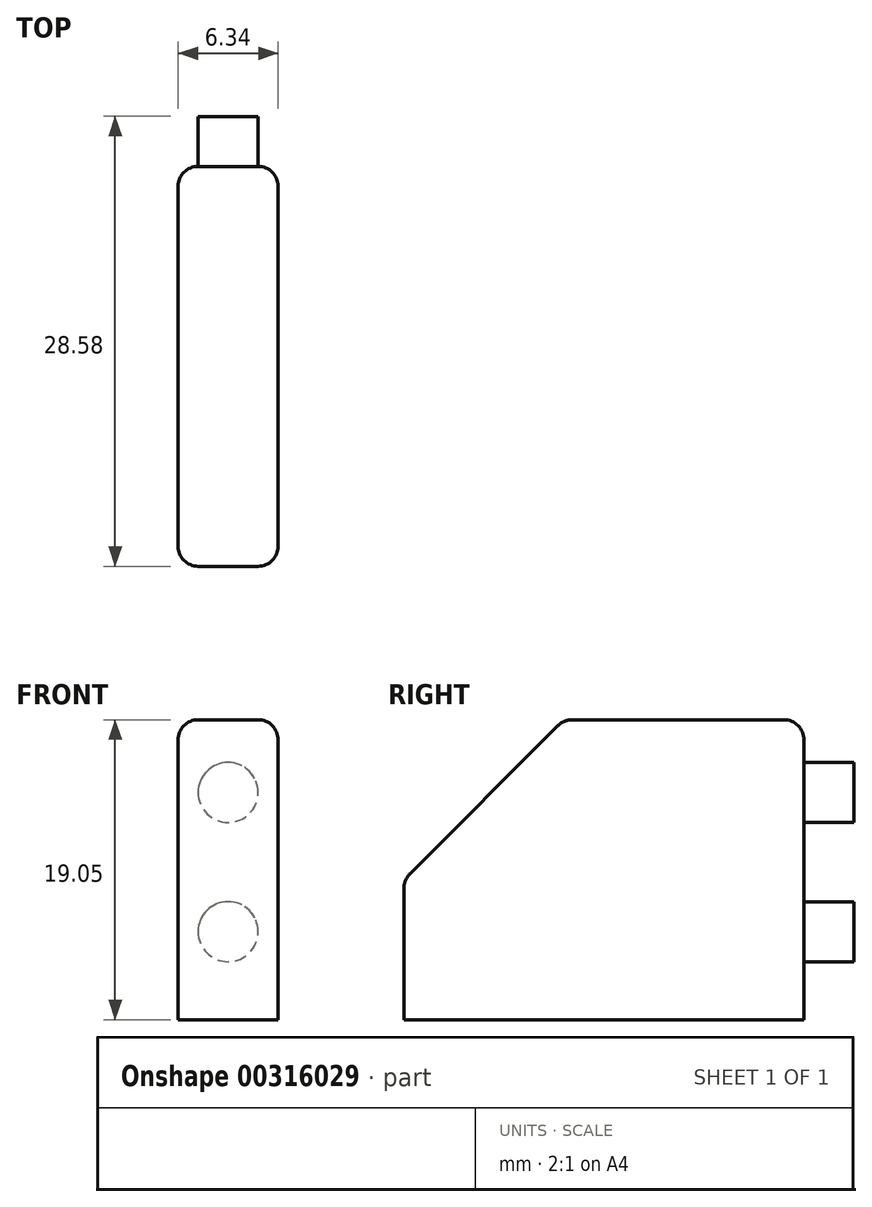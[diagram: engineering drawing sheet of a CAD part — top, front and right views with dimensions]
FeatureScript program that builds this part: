
annotation { "Feature Type Name" : "Feature", "Feature Type Description" : "" }
export const myFeature = defineFeature(function(context is Context, id is Id, definition is map)
    precondition{}
    {
        {
            var Q0;
            Q0=qCreatedBy(makeId("Top.planeOp"),FACE);
            var sketch = newSketch(context, id + "F0", { "sketchPlane" : qUnion([Q0])});
            skLineSegment(sketch, "E0.bottom", {"start": v(3.18, 12.7) * mm, "end": v(-3.17, 12.7) * mm});
            skLineSegment(sketch, "E0.top", {"start": v(3.18, -12.7) * mm, "end": v(-3.18, -12.7) * mm});
            skLineSegment(sketch, "E0.left", {"start": v(3.18, 12.7) * mm, "end": v(3.18, -12.7) * mm});
            skLineSegment(sketch, "E0.right", {"start": v(-3.17, 12.7) * mm, "end": v(-3.18, -12.7) * mm});
            skPoint(sketch, "E0.middle", {"position": v(0, 0) * mm});
            skSolve(sketch);
        }
        {
            var Q0;
            Q0 = qSketchRegion(id + "F0", true);
            extrude(context, id + "F1", {"entities" : qUnion([Q0]), "depth" : 19.05 * mm});
        }
        {
            var Q0;
            Q0=makeQuery(id+"F1.opExtrude","CAP_EDGE",EDGE,{"disambiguationData":[OSD([sQuery(id+"F0.wireOp",EDGE,"E0.top")])],"isStart":false});
            chamfer(context, id + "F2", {"entities" : qUnion([Q0]), "width" : 10.16 * mm, "tangentPropagation" : true});
        }
        {
            var Q0;
            Q0=makeQuery(id+"F1.opExtrude","CAP_EDGE",EDGE,{"disambiguationData":[OSD([sQuery(id+"F0.wireOp",EDGE,"E0.bottom")])],"isStart":false});
            var Q1;
            {var subQ0=sQuery(id+"F0.wireOp",EDGE,"E0.top");Q1=makeQuery(id+"F2.opChamfer","BLEND_EDGE",EDGE,{"blendedFrom":[makeQuery(id+"F1.opExtrude","CAP_EDGE",EDGE,{"disambiguationData":[OSD([subQ0])],"isStart":false}),makeQuery(id+"F1.opExtrude","CAP_FACE",FACE,{"disambiguationData":[OSD([sQuery(id+"F0.wireOp",EDGE,"E0.bottom"),subQ0,sQuery(id+"F0.wireOp",EDGE,"E0.left"),sQuery(id+"F0.wireOp",EDGE,"E0.right")])],"isStart":false})],"blendedInto":[makeQuery(id+"F1.opExtrude","CAP_FACE",FACE,{"disambiguationData":[OSD([sQuery(id+"F0.wireOp",EDGE,"E0.bottom"),subQ0,sQuery(id+"F0.wireOp",EDGE,"E0.left"),sQuery(id+"F0.wireOp",EDGE,"E0.right")])],"isStart":false})]});}
            var Q2;
            {var subQ0=sQuery(id+"F0.wireOp",EDGE,"E0.top");Q2=makeQuery(id+"F2.opChamfer","BLEND_EDGE",EDGE,{"blendedFrom":[makeQuery(id+"F1.opExtrude","CAP_EDGE",EDGE,{"disambiguationData":[OSD([subQ0])],"isStart":false}),makeQuery(id+"F1.opExtrude","SWEPT_FACE",FACE,{"disambiguationData":[OSD([subQ0])]})],"blendedInto":[makeQuery(id+"F1.opExtrude","SWEPT_FACE",FACE,{"disambiguationData":[OSD([subQ0])]})]});}
            fillet(context, id + "F3", {"entities" : qUnion([Q0, Q1, Q2]), "radius" : 1.27 * mm, "tangentPropagation" : true, "allowEdgeOverflow" : false});
        }
        {
            var Q0;
            Q0=makeQuery(id+"F1.opExtrude","SWEPT_EDGE",EDGE,{"disambiguationData":[OSD([sQuery(id+"F0.wireOp",EDGE,"E0.top"),sQuery(id+"F0.wireOp",EDGE,"E0.left")])]});
            var Q1;
            Q1=makeQuery(id+"F2.opChamfer","BLEND_EDGE",EDGE,{"blendedFrom":[makeQuery(id+"F1.opExtrude","CAP_EDGE",EDGE,{"disambiguationData":[OSD([sQuery(id+"F0.wireOp",EDGE,"E0.top")])],"isStart":false}),makeQuery(id+"F1.opExtrude","SWEPT_FACE",FACE,{"disambiguationData":[OSD([sQuery(id+"F0.wireOp",EDGE,"E0.left")])]})],"blendedInto":[makeQuery(id+"F1.opExtrude","SWEPT_FACE",FACE,{"disambiguationData":[OSD([sQuery(id+"F0.wireOp",EDGE,"E0.left")])]})]});
            var Q2;
            Q2=makeQuery(id+"F1.opExtrude","SWEPT_EDGE",EDGE,{"disambiguationData":[OSD([sQuery(id+"F0.wireOp",EDGE,"E0.top"),sQuery(id+"F0.wireOp",EDGE,"E0.right")])]});
            var Q3;
            Q3=makeQuery(id+"F2.opChamfer","BLEND_EDGE",EDGE,{"blendedFrom":[makeQuery(id+"F1.opExtrude","CAP_EDGE",EDGE,{"disambiguationData":[OSD([sQuery(id+"F0.wireOp",EDGE,"E0.top")])],"isStart":false}),makeQuery(id+"F1.opExtrude","SWEPT_FACE",FACE,{"disambiguationData":[OSD([sQuery(id+"F0.wireOp",EDGE,"E0.right")])]})],"blendedInto":[makeQuery(id+"F1.opExtrude","SWEPT_FACE",FACE,{"disambiguationData":[OSD([sQuery(id+"F0.wireOp",EDGE,"E0.right")])]})]});
            var Q4;
            {var subQ0=sQuery(id+"F0.wireOp",EDGE,"E0.top");Q4=makeQuery(id+"F3.opFillet","BLEND_EDGE",EDGE,{"blendedFrom":[makeQuery(id+"F2.opChamfer","BLEND_EDGE",EDGE,{"blendedFrom":[makeQuery(id+"F1.opExtrude","CAP_EDGE",EDGE,{"disambiguationData":[OSD([subQ0])],"isStart":false}),makeQuery(id+"F1.opExtrude","SWEPT_FACE",FACE,{"disambiguationData":[OSD([subQ0])]})],"blendedInto":[makeQuery(id+"F1.opExtrude","SWEPT_FACE",FACE,{"disambiguationData":[OSD([subQ0])]})]}),makeQuery(id+"F1.opExtrude","SWEPT_FACE",FACE,{"disambiguationData":[OSD([sQuery(id+"F0.wireOp",EDGE,"E0.right")])]})],"blendedInto":[makeQuery(id+"F1.opExtrude","SWEPT_FACE",FACE,{"disambiguationData":[OSD([sQuery(id+"F0.wireOp",EDGE,"E0.right")])]})]});}
            var Q5;
            {var subQ0=sQuery(id+"F0.wireOp",EDGE,"E0.top");Q5=makeQuery(id+"F3.opFillet","BLEND_EDGE",EDGE,{"blendedFrom":[makeQuery(id+"F2.opChamfer","BLEND_EDGE",EDGE,{"blendedFrom":[makeQuery(id+"F1.opExtrude","CAP_EDGE",EDGE,{"disambiguationData":[OSD([subQ0])],"isStart":false}),makeQuery(id+"F1.opExtrude","SWEPT_FACE",FACE,{"disambiguationData":[OSD([subQ0])]})],"blendedInto":[makeQuery(id+"F1.opExtrude","SWEPT_FACE",FACE,{"disambiguationData":[OSD([subQ0])]})]}),makeQuery(id+"F1.opExtrude","SWEPT_FACE",FACE,{"disambiguationData":[OSD([sQuery(id+"F0.wireOp",EDGE,"E0.left")])]})],"blendedInto":[makeQuery(id+"F1.opExtrude","SWEPT_FACE",FACE,{"disambiguationData":[OSD([sQuery(id+"F0.wireOp",EDGE,"E0.left")])]})]});}
            var Q6;
            {var subQ0=sQuery(id+"F0.wireOp",EDGE,"E0.left");var subQ1=sQuery(id+"F0.wireOp",EDGE,"E0.top");Q6=makeQuery(id+"F3.opFillet","BLEND_EDGE",EDGE,{"blendedFrom":[makeQuery(id+"F2.opChamfer","BLEND_EDGE",EDGE,{"blendedFrom":[makeQuery(id+"F1.opExtrude","CAP_EDGE",EDGE,{"disambiguationData":[OSD([subQ1])],"isStart":false}),makeQuery(id+"F1.opExtrude","CAP_FACE",FACE,{"disambiguationData":[OSD([sQuery(id+"F0.wireOp",EDGE,"E0.bottom"),subQ1,subQ0,sQuery(id+"F0.wireOp",EDGE,"E0.right")])],"isStart":false})],"blendedInto":[makeQuery(id+"F1.opExtrude","CAP_FACE",FACE,{"disambiguationData":[OSD([sQuery(id+"F0.wireOp",EDGE,"E0.bottom"),subQ1,subQ0,sQuery(id+"F0.wireOp",EDGE,"E0.right")])],"isStart":false})]}),makeQuery(id+"F1.opExtrude","SWEPT_FACE",FACE,{"disambiguationData":[OSD([subQ0])]})],"blendedInto":[makeQuery(id+"F1.opExtrude","SWEPT_FACE",FACE,{"disambiguationData":[OSD([subQ0])]})]});}
            var Q7;
            Q7=makeQuery(id+"F1.opExtrude","CAP_EDGE",EDGE,{"disambiguationData":[OSD([sQuery(id+"F0.wireOp",EDGE,"E0.left")])],"isStart":false});
            var Q8;
            {var subQ0=sQuery(id+"F0.wireOp",EDGE,"E0.right");var subQ1=sQuery(id+"F0.wireOp",EDGE,"E0.top");Q8=makeQuery(id+"F3.opFillet","BLEND_EDGE",EDGE,{"blendedFrom":[makeQuery(id+"F2.opChamfer","BLEND_EDGE",EDGE,{"blendedFrom":[makeQuery(id+"F1.opExtrude","CAP_EDGE",EDGE,{"disambiguationData":[OSD([subQ1])],"isStart":false}),makeQuery(id+"F1.opExtrude","CAP_FACE",FACE,{"disambiguationData":[OSD([sQuery(id+"F0.wireOp",EDGE,"E0.bottom"),subQ1,sQuery(id+"F0.wireOp",EDGE,"E0.left"),subQ0])],"isStart":false})],"blendedInto":[makeQuery(id+"F1.opExtrude","CAP_FACE",FACE,{"disambiguationData":[OSD([sQuery(id+"F0.wireOp",EDGE,"E0.bottom"),subQ1,sQuery(id+"F0.wireOp",EDGE,"E0.left"),subQ0])],"isStart":false})]}),makeQuery(id+"F1.opExtrude","SWEPT_FACE",FACE,{"disambiguationData":[OSD([subQ0])]})],"blendedInto":[makeQuery(id+"F1.opExtrude","SWEPT_FACE",FACE,{"disambiguationData":[OSD([subQ0])]})]});}
            var Q9;
            Q9=makeQuery(id+"F1.opExtrude","CAP_EDGE",EDGE,{"disambiguationData":[OSD([sQuery(id+"F0.wireOp",EDGE,"E0.right")])],"isStart":false});
            var Q10;
            Q10=makeQuery(id+"F3.opFillet","BLEND_EDGE",EDGE,{"blendedFrom":[makeQuery(id+"F1.opExtrude","CAP_EDGE",EDGE,{"disambiguationData":[OSD([sQuery(id+"F0.wireOp",EDGE,"E0.bottom")])],"isStart":false}),makeQuery(id+"F1.opExtrude","SWEPT_FACE",FACE,{"disambiguationData":[OSD([sQuery(id+"F0.wireOp",EDGE,"E0.right")])]})],"blendedInto":[makeQuery(id+"F1.opExtrude","SWEPT_FACE",FACE,{"disambiguationData":[OSD([sQuery(id+"F0.wireOp",EDGE,"E0.right")])]})]});
            var Q11;
            Q11=makeQuery(id+"F3.opFillet","BLEND_EDGE",EDGE,{"blendedFrom":[makeQuery(id+"F1.opExtrude","CAP_EDGE",EDGE,{"disambiguationData":[OSD([sQuery(id+"F0.wireOp",EDGE,"E0.bottom")])],"isStart":false}),makeQuery(id+"F1.opExtrude","SWEPT_FACE",FACE,{"disambiguationData":[OSD([sQuery(id+"F0.wireOp",EDGE,"E0.left")])]})],"blendedInto":[makeQuery(id+"F1.opExtrude","SWEPT_FACE",FACE,{"disambiguationData":[OSD([sQuery(id+"F0.wireOp",EDGE,"E0.left")])]})]});
            var Q12;
            Q12=makeQuery(id+"F1.opExtrude","SWEPT_EDGE",EDGE,{"disambiguationData":[OSD([sQuery(id+"F0.wireOp",EDGE,"E0.bottom"),sQuery(id+"F0.wireOp",EDGE,"E0.left")])]});
            var Q13;
            Q13=makeQuery(id+"F1.opExtrude","SWEPT_EDGE",EDGE,{"disambiguationData":[OSD([sQuery(id+"F0.wireOp",EDGE,"E0.bottom"),sQuery(id+"F0.wireOp",EDGE,"E0.right")])]});
            fillet(context, id + "F4", {"entities" : qUnion([Q0, Q1, Q2, Q3, Q4, Q5, Q6, Q7, Q8, Q9, Q10, Q11, Q12, Q13]), "radius" : 1.27 * mm, "tangentPropagation" : true, "allowEdgeOverflow" : false});
        }
        {
            var Q0;
            Q0=makeQuery(id+"F1.opExtrude","SWEPT_FACE",FACE,{"disambiguationData":[OSD([sQuery(id+"F0.wireOp",EDGE,"E0.bottom")])]});
            var sketch = newSketch(context, id + "F5", { "sketchPlane" : qUnion([Q0])});
            skCircle(sketch, "E1", {"center": v(0, 14.43) * mm, "radius": 1.9 * mm});
            skCircle(sketch, "E2", {"center": v(0, 5.59) * mm, "radius": 1.9 * mm});
            skSolve(sketch);
        }
        {
            var Q0;
            Q0 = qSketchRegion(id + "F5", true);
            extrude(context, id + "F6", {"entities" : qUnion([Q0]), "operationType" : NewBodyOperationType.ADD, "depth" : 3.17 * mm});
        }
    });
